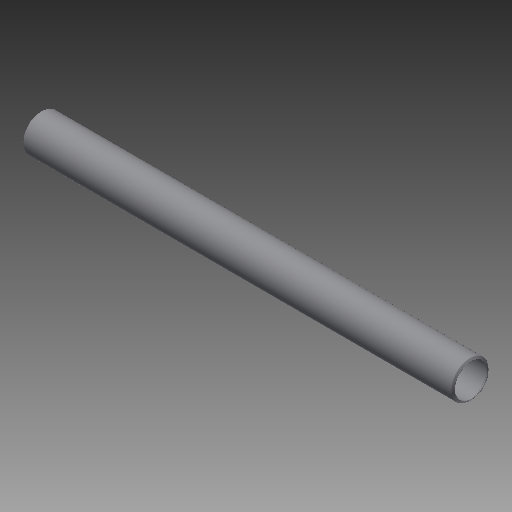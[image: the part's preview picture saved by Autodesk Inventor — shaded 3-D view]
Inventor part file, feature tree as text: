
AUTODESK INVENTOR PART (.ipt)
format: ipt  version: 2019.4 (Build 234330000, 330)  size: 138,752 bytes
history: native  units: in
note: dims shown in document units (in); Inventor stores cm internally (conversion verified against a paired STEP export)
features: other x42, revolve x1, sketch x1
ambient origin geometry x8: Origin, YZ Plane, XZ Plane, XY Plane, X Axis, Y Axis, Z Axis, Center Point
bodies: Solid1 (feature_tree)
feature tree (44):
  revolve  "Revolution1"  [1 undecoded]
  other  "cp1_XY"
  other  "cp1_YZ"
  other  "cp1_ZX"
  other  "cp1_X"
  other  "cp1_Y"
  other  "cp1_Z"
  other  "cp1_Center"
  other  "cp2_XY"
  other  "cp2_YZ"
  other  "cp2_ZX"
  other  "cp2_X"
  other  "cp2_Y"
  other  "cp2_Z"
  other  "cp2_Center"
  other  "cp3_XY"
  other  "cp3_YZ"
  other  "cp3_ZX"
  other  "cp3_X"
  other  "cp3_Y"
  other  "cp3_Z"
  other  "cp3_Center"
  other  "cp4_XY"
  other  "cp4_YZ"
  other  "cp4_ZX"
  other  "cp4_X"
  other  "cp4_Y"
  other  "cp4_Z"
  other  "cp4_Center"
  other  "tube_front_XY"
  other  "tube_front_YZ"
  other  "tube_front_ZX"
  other  "tube_front_X"
  other  "tube_front_Y"
  other  "tube_front_Z"
  other  "tube_front_Center"
  other  "tube_rear_XY"
  other  "tube_rear_YZ"
  other  "tube_rear_ZX"
  other  "tube_rear_X"
  other  "tube_rear_Y"
  other  "tube_rear_Z"
  other  "tube_rear_Center"
  sketch  "Sketch_1"  dims[d0=360.0deg]
note: 1 required parameter value undecoded (feature->parameter linkage not recoverable at this tier; creation-order binding heuristic only, values carry confidence <= 0.55)
